# Revit family: ROSENBERG_R
name_source: partatom
category: Wyposażenie mechaniczne
revit_build: Autodesk Revit 2017 (Build: 20160225_1515(x64)
units: mm (PartAtom-declared; Revit-internal decimal feet)

## family parameters
Numer OmniClass = 23.75.00.00
Oparty na płaszczyźnie roboczej = Nie
Punkt obliczania pomieszczeń = Nie
Tnij formami wycięć po wczytaniu = Nie
Typ części = Dzieli na
Tytuł OmniClass = Climate Control (HVAC)
Współdzielony = Tak
Wymiar okrągłego złącza = Użyj średnicy
Zawsze pionowo = Tak

## types (14) — shared parameters
Date = 10.2018
Frequence = 50 Hz
Materiał = <Wg kategorii>
Opis = Wentylator kanałowy
Producent = Rosenberg
URL = https://www.rosenberg.pl
Version = 1
param.Puszka.wysokość = 87 mm  [stored 0.285433 ft]

## per-type parameters (varying)
| type | Air_flow | Current | Diameter_connector | Power | Pressure | Protection_Class | Voltage | Weight | param.F1 | param.Otwór.wentylator | param.Puszka.szerokość | param.Wentylator.H_kołnierz | param.Wentylator.długość | param.Wentylator.szerokość | param.b1 |
| 200.3CF | 471.0 m³/h | 0 A | 200 mm  [stored 0.656168 ft] | 96 W | 213.0 Pa | IP44 | 230 V | 3.50 kg | 160 mm | 195 mm | 41 mm | 25 mm  [stored 0.082021 ft] | 240 mm | 341 mm | 60 mm |
| 100.2CA | 0.0 m³/h | 0 A | 100 mm  [stored 0.328084 ft] | 28 W | 0.0 Pa | IP44 | 230 V | 2.00 kg | 124 mm | 95 mm  [stored 0.31168 ft] | 41 mm | 25 mm  [stored 0.082021 ft] | 186 mm | 243 mm | 47 mm |
| 125.2CA | 0.0 m³/h | 0 A | 125 mm | 28 W | 0.0 Pa | IP44 | 230 V | 2.10 kg | 131 mm | 120 mm  [stored 0.393701 ft] | 41 mm | 25 mm  [stored 0.082021 ft] | 196 mm | 243 mm | 49 mm |
| 150.3CA | 270.0 m³/h | 0 A | 150 mm | 50 W | 189.0 Pa | IP44 | 230 V | 3.00 kg | 127 mm | 145 mm | 41 mm | 25 mm  [stored 0.082021 ft] | 190 mm | 341 mm | 48 mm |
| 160.3CA | 254.0 m³/h | 0 A | 160 mm | 49 W | 205.0 Pa | IP44 | 230 V | 3.00 kg | 133 mm | 155 mm  [stored 0.50853 ft] | 41 mm | 25 mm  [stored 0.082021 ft] | 200 mm  [stored 0.656168 ft] | 341 mm | 50 mm  [stored 0.164042 ft] |
| 160 L.3CF | 488.0 m³/h | 0 A | 160 mm | 91 W | 196.0 Pa | IP44 | 230 V | 3.50 kg | 133 mm | 155 mm  [stored 0.50853 ft] | 41 mm | 25 mm  [stored 0.082021 ft] | 200 mm  [stored 0.656168 ft] | 341 mm | 50 mm  [stored 0.164042 ft] |
| 250.3CF | 506.0 m³/h | 0 A | 250 mm | 103 W | 225.0 Pa | IP44 | 230 V | 3.80 kg | 153 mm | 245 mm  [stored 0.803806 ft] | 41 mm | 30 mm  [stored 0.0984252 ft] | 230 mm | 341 mm | 58 mm |
| 355 M.5FA | 1325.0 m³/h | 1 A | 355 mm | 270 W | 256.0 Pa | IP54 | 230 V | 15.60 kg | 263 mm | 350 mm | 41 mm | 35 mm  [stored 0.114829 ft] | 395 mm | 490 mm | 99 mm |
| 315 M.3EF | 691.0 m³/h | 1 A | 315 mm | 200 W | 413.0 Pa | IP44 | 230 V | 6.20 kg | 157 mm | 310 mm | 41 mm | 30 mm  [stored 0.0984252 ft] | 235 mm  [stored 0.770997 ft] | 405 mm | 59 mm |
| 315.3EF | 702.0 m³/h | 1 A | 315 mm | 180 W | 346.0 Pa | IP44 | 230 V | 6.20 kg | 173 mm | 310 mm | 41 mm | 30 mm  [stored 0.0984252 ft] | 260 mm | 405 mm | 65 mm |
| 250 L.3DF | 465.0 m³/h | 1 A | 250 mm | 120 W | 292.0 Pa | IP44 | 230 V | 4.20 kg | 153 mm | 245 mm  [stored 0.803806 ft] | 41 mm | 30 mm  [stored 0.0984252 ft] | 230 mm | 341 mm | 58 mm |
| 315.4EC Zone 2 | 0.0 m³/h | 0 A | 315 mm | 100 W | 0.0 Pa | IP44 | 400 V | 7.00 kg | 173 mm | 310 mm | 41 mm | 35 mm  [stored 0.114829 ft] | 260 mm | 405 mm | 65 mm |
| 400 LE STAHL | 3236.0 m³/h | 3 A | 400 mm | 700 W | 288.0 Pa | IP54 | 230 V | 31.00 kg | 400 mm | 395 mm | 43 mm | 35 mm  [stored 0.114829 ft] | 600 mm | 570 mm | 150 mm |
| 400 LD STAHL | 3309.0 m³/h | 2 A | 400 mm | 670 W | 312.0 Pa | IP54 | 400 V | 31.00 kg | 400 mm | 395 mm | 43 mm | 35 mm  [stored 0.114829 ft] | 600 mm | 570 mm | 150 mm |

note: column(s) folded — value = type name in every type: Model

note: [stored X ft] marks values corroborated as IEEE doubles in the binary element streams (Revit-internal decimal feet)

## geometry (parser evidence)
native form markers: Blend x4, Sweep x5
no freeform markers — native parametric forms only
